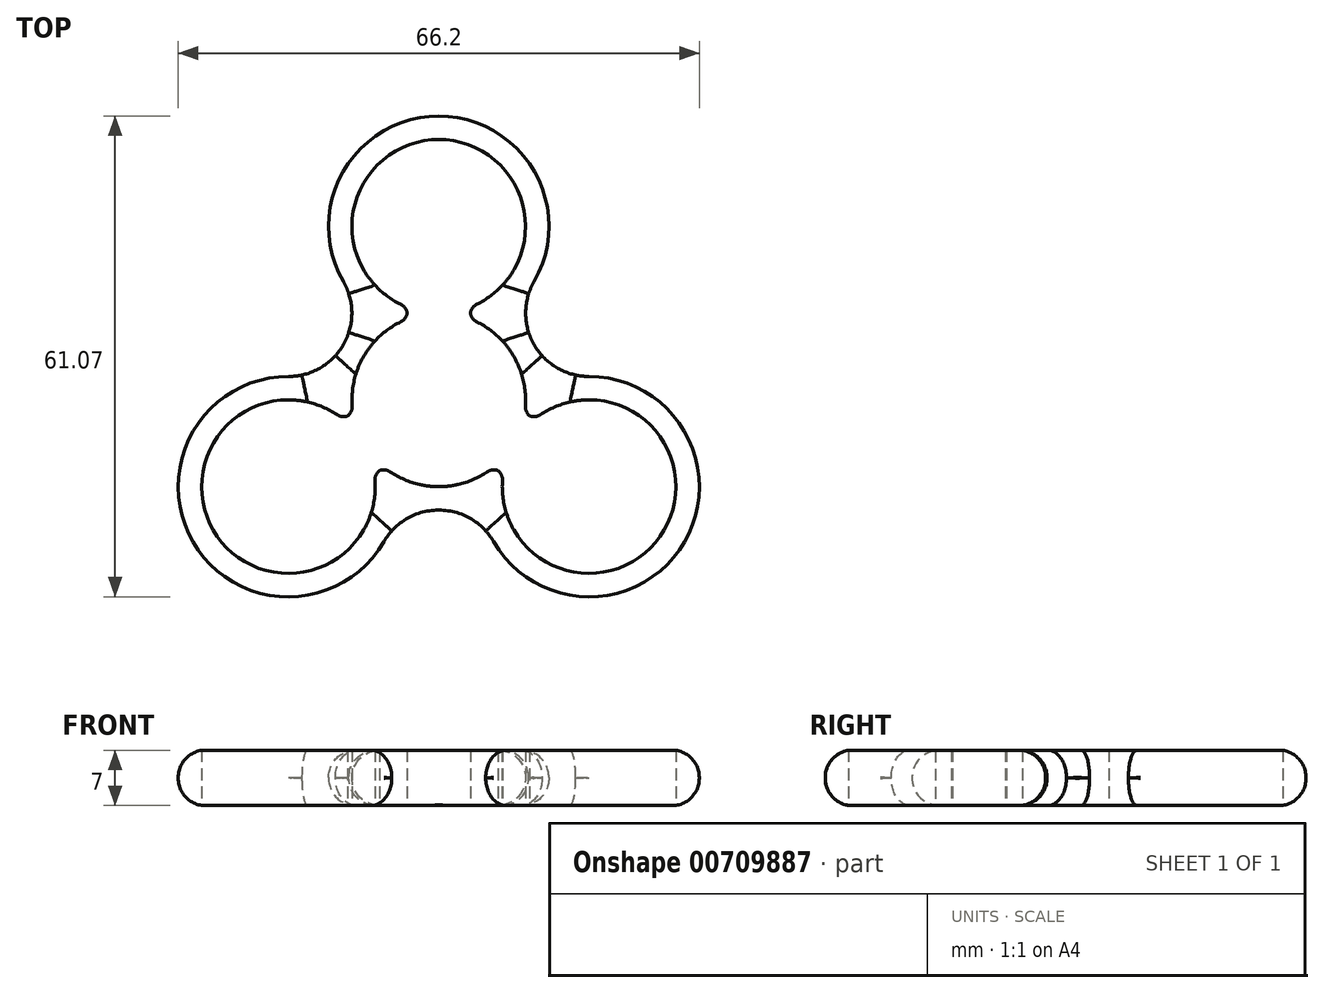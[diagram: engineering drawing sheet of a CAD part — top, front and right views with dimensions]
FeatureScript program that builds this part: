
annotation { "Feature Type Name" : "Feature", "Feature Type Description" : "" }
export const myFeature = defineFeature(function(context is Context, id is Id, definition is map)
    precondition{}
    {
        {
            var Q0;
            Q0=qCreatedBy(makeId("Top.planeOp"),FACE);
            var sketch = newSketch(context, id + "F0", { "sketchPlane" : qUnion([Q0])});
            skArc(sketch, "E0", {"start": v(-4, 10.27) * mm, "mid": v(-9.55, 5.51) * mm, "end": v(-10.9, -1.67) * mm});
            skArc(sketch, "E1", {"start": v(4, 11.78) * mm, "mid": v(0, 33.08) * mm, "end": v(-4, 11.78) * mm});
            skArc(sketch, "E2", {"start": v(4, 8.63) * mm, "mid": v(0, 36.05) * mm, "end": v(-4, 8.63) * mm});
            skArc(sketch, "E3", {"start": v(-4, 13.42) * mm, "mid": v(-12.12, 7) * mm, "end": v(-13.62, -3.24) * mm});
            skLineSegment(sketch, "E4.bottom", {"start": v(4, 7.03) * mm, "end": v(-4, 7.02) * mm});
            skLineSegment(sketch, "E4.top", {"start": v(4, 15.03) * mm, "end": v(-4, 15.03) * mm});
            skLineSegment(sketch, "E4.left", {"start": v(4, 7.03) * mm, "end": v(4, 15.03) * mm});
            skLineSegment(sketch, "E4.right", {"start": v(-4, 7.03) * mm, "end": v(-4, 15.03) * mm});
            skPoint(sketch, "E4.middle", {"position": v(0, 11.03) * mm});
            skArc(sketch, "E5.1.0", {"start": v(-9.48, -0.85) * mm, "mid": v(-31.22, -18.02) * mm, "end": v(-5.48, -7.78) * mm});
            skArc(sketch, "E5.1.1", {"start": v(-12.2, -2.42) * mm, "mid": v(-28.64, -16.54) * mm, "end": v(-8.2, -9.35) * mm});
            skLineSegment(sketch, "E5.1.2", {"start": v(-15.01, -4.05) * mm, "end": v(-11.01, -10.98) * mm});
            skLineSegment(sketch, "E5.1.3", {"start": v(-8.08, -0.05) * mm, "end": v(-15.01, -4.05) * mm});
            skLineSegment(sketch, "E5.1.4", {"start": v(-4.08, -6.98) * mm, "end": v(-11.01, -10.98) * mm});
            skLineSegment(sketch, "E5.1.5", {"start": v(-8.08, -0.05) * mm, "end": v(-4.08, -6.98) * mm});
            skArc(sketch, "E5.2.0", {"start": v(5.48, -7.78) * mm, "mid": v(31.22, -18.03) * mm, "end": v(9.48, -0.85) * mm});
            skArc(sketch, "E5.2.1", {"start": v(8.2, -9.35) * mm, "mid": v(28.64, -16.54) * mm, "end": v(12.2, -2.42) * mm});
            skLineSegment(sketch, "E5.2.2", {"start": v(11.01, -10.98) * mm, "end": v(15.01, -4.05) * mm});
            skLineSegment(sketch, "E5.2.3", {"start": v(4.08, -6.98) * mm, "end": v(11.01, -10.98) * mm});
            skLineSegment(sketch, "E5.2.4", {"start": v(8.08, -0.05) * mm, "end": v(15.01, -4.05) * mm});
            skLineSegment(sketch, "E5.2.5", {"start": v(4.08, -6.98) * mm, "end": v(8.08, -0.05) * mm});
            skArc(sketch, "E6.trimOffspring", {"start": v(-9.62, -10.17) * mm, "mid": v(0, -14) * mm, "end": v(9.62, -10.17) * mm});
            skArc(sketch, "E7.trimOffspring", {"start": v(13.62, -3.24) * mm, "mid": v(12.12, 7) * mm, "end": v(4, 13.42) * mm});
            skArc(sketch, "E8.trimOffspring", {"start": v(10.9, -1.67) * mm, "mid": v(9.55, 5.51) * mm, "end": v(4, 10.27) * mm});
            skArc(sketch, "E9.trimOffspring", {"start": v(-6.9, -8.6) * mm, "mid": v(0, -11.03) * mm, "end": v(6.9, -8.6) * mm});
            skSolve(sketch);
        }
        {
            var Q0;
            {var subQ0=sQuery(id+"F0.wireOp",EDGE,"E3");var subQ1=sQuery(id+"F0.wireOp",EDGE,"E1");var subQ2=makeQuery(id+"F0.imprint","INTERSECT",VERTEX,{"derivedFrom":[subQ1,subQ0]});Q0=makeQuery(id+"F0.imprint","IMPRINT",FACE,{"disambiguationData":[TD([[makeQuery(id+"F0.imprint","IMPRINT",EDGE,{"disambiguationData":[TD([[subQ2,1.0]])],"derivedFrom":subQ1}),-1.0]])]});}
            var Q1;
            {var subQ1=sQuery(id+"F0.wireOp",EDGE,"E0");var subQ5=sQuery(id+"F0.wireOp",EDGE,"E2");var subQ6=makeQuery(id+"F0.imprint","INTERSECT",VERTEX,{"disambiguationData":[OD(0.0)],"derivedFrom":[subQ1,subQ5]});Q1=makeQuery(id+"F0.imprint","IMPRINT",FACE,{"disambiguationData":[TD([[makeQuery(id+"F0.imprint","IMPRINT",EDGE,{"disambiguationData":[TD([[subQ6,-1.0]])],"derivedFrom":subQ1}),-1.0]])]});}
            var Q2;
            {var subQ5=sQuery(id+"F0.wireOp",EDGE,"E4.right");var subQ7=sQuery(id+"F0.wireOp",EDGE,"E0");var subQ8=makeQuery(id+"F0.imprint","INTERSECT",VERTEX,{"derivedFrom":[subQ7,subQ5]});Q2=makeQuery(id+"F0.imprint","IMPRINT",FACE,{"disambiguationData":[TD([[makeQuery(id+"F0.imprint","IMPRINT",EDGE,{"disambiguationData":[TD([[subQ8,-1.0]])],"derivedFrom":subQ7}),-1.0]])]});}
            var Q3;
            {var subQ0=sQuery(id+"F0.wireOp",EDGE,"E2");var subQ1=sQuery(id+"F0.wireOp",EDGE,"E0");var subQ2=makeQuery(id+"F0.imprint","INTERSECT",VERTEX,{"disambiguationData":[OD(0.0)],"derivedFrom":[subQ1,subQ0]});Q3=makeQuery(id+"F0.imprint","IMPRINT",FACE,{"disambiguationData":[TD([[makeQuery(id+"F0.imprint","IMPRINT",EDGE,{"disambiguationData":[TD([[subQ2,1.0]])],"derivedFrom":subQ1}),-1.0]])]});}
            var Q4;
            {var subQ0=sQuery(id+"F0.wireOp",EDGE,"E2");var subQ1=sQuery(id+"F0.wireOp",EDGE,"E0");var subQ2=makeQuery(id+"F0.imprint","INTERSECT",VERTEX,{"disambiguationData":[OD(1.0)],"derivedFrom":[subQ1,subQ0]});Q4=makeQuery(id+"F0.imprint","IMPRINT",FACE,{"disambiguationData":[TD([[makeQuery(id+"F0.imprint","IMPRINT",EDGE,{"disambiguationData":[TD([[subQ2,-1.0]])],"derivedFrom":subQ1}),-1.0]])]});}
            var Q5;
            {var subQ0=sQuery(id+"F0.wireOp",EDGE,"E5.1.0");var subQ1=sQuery(id+"F0.wireOp",EDGE,"E0");var subQ2=makeQuery(id+"F0.imprint","INTERSECT",VERTEX,{"disambiguationData":[OD(1.0)],"derivedFrom":[subQ1,subQ0]});Q5=makeQuery(id+"F0.imprint","IMPRINT",FACE,{"disambiguationData":[TD([[makeQuery(id+"F0.imprint","IMPRINT",EDGE,{"disambiguationData":[TD([[subQ2,-1.0]])],"derivedFrom":subQ1}),-1.0]])]});}
            var Q6;
            {var subQ1=sQuery(id+"F0.wireOp",EDGE,"E0");var subQ5=sQuery(id+"F0.wireOp",EDGE,"E5.2.0");var subQ6=makeQuery(id+"F0.imprint","INTERSECT",VERTEX,{"disambiguationData":[OD(1.0)],"derivedFrom":[subQ1,subQ5]});Q6=makeQuery(id+"F0.imprint","IMPRINT",FACE,{"disambiguationData":[TD([[makeQuery(id+"F0.imprint","IMPRINT",EDGE,{"disambiguationData":[TD([[subQ6,-1.0]])],"derivedFrom":subQ1}),-1.0]])]});}
            var Q7;
            {var subQ1=sQuery(id+"F0.wireOp",EDGE,"E0");var subQ6=sQuery(id+"F0.wireOp",EDGE,"E5.2.0");var subQ8=makeQuery(id+"F0.imprint","INTERSECT",VERTEX,{"disambiguationData":[OD(0.0)],"derivedFrom":[subQ1,subQ6]});Q7=makeQuery(id+"F0.imprint","IMPRINT",FACE,{"disambiguationData":[TD([[makeQuery(id+"F0.imprint","IMPRINT",EDGE,{"disambiguationData":[TD([[subQ8,1.0]])],"derivedFrom":subQ1}),-1.0]])]});}
            var Q8;
            {var subQ0=sQuery(id+"F0.wireOp",EDGE,"E6.trimOffspring");var subQ1=sQuery(id+"F0.wireOp",EDGE,"E5.2.0");var subQ2=makeQuery(id+"F0.imprint","INTERSECT",VERTEX,{"derivedFrom":[subQ1,subQ0]});Q8=makeQuery(id+"F0.imprint","IMPRINT",FACE,{"disambiguationData":[TD([[makeQuery(id+"F0.imprint","IMPRINT",EDGE,{"disambiguationData":[TD([[subQ2,-1.0]])],"derivedFrom":subQ1}),1.0]])]});}
            var Q9;
            {var subQ0=sQuery(id+"F0.wireOp",EDGE,"E5.1.0");var subQ1=sQuery(id+"F0.wireOp",EDGE,"E3");var subQ2=makeQuery(id+"F0.imprint","INTERSECT",VERTEX,{"derivedFrom":[subQ1,subQ0]});Q9=makeQuery(id+"F0.imprint","IMPRINT",FACE,{"disambiguationData":[TD([[makeQuery(id+"F0.imprint","IMPRINT",EDGE,{"disambiguationData":[TD([[subQ2,-1.0]])],"derivedFrom":subQ1}),-1.0]])]});}
            var Q10;
            {var subQ0=sQuery(id+"F0.wireOp",EDGE,"E5.1.4");var subQ5=sQuery(id+"F0.wireOp",EDGE,"E0");var subQ6=makeQuery(id+"F0.imprint","INTERSECT",VERTEX,{"derivedFrom":[subQ5,subQ0]});Q10=makeQuery(id+"F0.imprint","IMPRINT",FACE,{"disambiguationData":[TD([[makeQuery(id+"F0.imprint","IMPRINT",EDGE,{"disambiguationData":[TD([[subQ6,-1.0]])],"derivedFrom":subQ5}),-1.0]])]});}
            var Q11;
            {var subQ5=sQuery(id+"F0.wireOp",EDGE,"E5.1.0");var subQ7=sQuery(id+"F0.wireOp",EDGE,"E0");var subQ8=makeQuery(id+"F0.imprint","INTERSECT",VERTEX,{"disambiguationData":[OD(0.0)],"derivedFrom":[subQ7,subQ5]});Q11=makeQuery(id+"F0.imprint","IMPRINT",FACE,{"disambiguationData":[TD([[makeQuery(id+"F0.imprint","IMPRINT",EDGE,{"disambiguationData":[TD([[subQ8,-1.0]])],"derivedFrom":subQ7}),-1.0]])]});}
            var Q12;
            {var subQ0=sQuery(id+"F0.wireOp",EDGE,"E7.trimOffspring");var subQ1=sQuery(id+"F0.wireOp",EDGE,"E2");var subQ2=makeQuery(id+"F0.imprint","INTERSECT",VERTEX,{"derivedFrom":[subQ1,subQ0]});Q12=makeQuery(id+"F0.imprint","IMPRINT",FACE,{"disambiguationData":[TD([[makeQuery(id+"F0.imprint","IMPRINT",EDGE,{"disambiguationData":[TD([[subQ2,1.0]])],"derivedFrom":subQ1}),-1.0]])]});}
            var Q13;
            {var subQ3=sQuery(id+"F0.wireOp",EDGE,"E1");var subQ5=sQuery(id+"F0.wireOp",EDGE,"E4.left");var subQ6=makeQuery(id+"F0.imprint","INTERSECT",VERTEX,{"derivedFrom":[subQ3,subQ5]});Q13=makeQuery(id+"F0.imprint","IMPRINT",FACE,{"disambiguationData":[TD([[makeQuery(id+"F0.imprint","IMPRINT",EDGE,{"disambiguationData":[TD([[subQ6,-1.0]])],"derivedFrom":subQ3}),-1.0]])]});}
            var Q14;
            {var subQ0=sQuery(id+"F0.wireOp",EDGE,"E7.trimOffspring");var subQ1=sQuery(id+"F0.wireOp",EDGE,"E5.2.0");var subQ2=makeQuery(id+"F0.imprint","INTERSECT",VERTEX,{"derivedFrom":[subQ1,subQ0]});Q14=makeQuery(id+"F0.imprint","IMPRINT",FACE,{"disambiguationData":[TD([[makeQuery(id+"F0.imprint","IMPRINT",EDGE,{"disambiguationData":[TD([[subQ2,-1.0]])],"derivedFrom":subQ1}),1.0]])]});}
            var Q15;
            {var subQ0=sQuery(id+"F0.wireOp",EDGE,"E6.trimOffspring");var subQ1=sQuery(id+"F0.wireOp",EDGE,"E5.2.0");var subQ2=makeQuery(id+"F0.imprint","INTERSECT",VERTEX,{"derivedFrom":[subQ1,subQ0]});Q15=makeQuery(id+"F0.imprint","IMPRINT",FACE,{"disambiguationData":[TD([[makeQuery(id+"F0.imprint","IMPRINT",EDGE,{"disambiguationData":[TD([[subQ2,1.0]])],"derivedFrom":subQ1}),1.0]])]});}
            var Q16;
            {var subQ0=sQuery(id+"F0.wireOp",EDGE,"E6.trimOffspring");var subQ1=sQuery(id+"F0.wireOp",EDGE,"E5.1.0");var subQ2=makeQuery(id+"F0.imprint","INTERSECT",VERTEX,{"derivedFrom":[subQ1,subQ0]});Q16=makeQuery(id+"F0.imprint","IMPRINT",FACE,{"disambiguationData":[TD([[makeQuery(id+"F0.imprint","IMPRINT",EDGE,{"disambiguationData":[TD([[subQ2,-1.0]])],"derivedFrom":subQ1}),-1.0]])]});}
            var Q17;
            {var subQ0=sQuery(id+"F0.wireOp",EDGE,"E6.trimOffspring");var subQ1=sQuery(id+"F0.wireOp",EDGE,"E5.1.0");var subQ2=makeQuery(id+"F0.imprint","INTERSECT",VERTEX,{"derivedFrom":[subQ1,subQ0]});Q17=makeQuery(id+"F0.imprint","IMPRINT",FACE,{"disambiguationData":[TD([[makeQuery(id+"F0.imprint","IMPRINT",EDGE,{"disambiguationData":[TD([[subQ2,-1.0]])],"derivedFrom":subQ1}),1.0]])]});}
            extrude(context, id + "F1", {"entities" : qUnion([Q0, Q1, Q2, Q3, Q4, Q5, Q6, Q7, Q8, Q9, Q10, Q11, Q12, Q13, Q14, Q15, Q16, Q17]), "depth" : 7 * mm, "offsetDistance" : 25 * mm});
        }
        {
            var Q0;
            Q0=makeQuery(id+"F1.opExtrude","SWEPT_EDGE",EDGE,{"disambiguationData":[OSD([sQuery(id+"F0.wireOp",EDGE,"E0"),sQuery(id+"F0.wireOp",EDGE,"E4.right")])]});
            var Q1;
            Q1=makeQuery(id+"F1.opExtrude","SWEPT_EDGE",EDGE,{"disambiguationData":[OSD([sQuery(id+"F0.wireOp",EDGE,"E1"),sQuery(id+"F0.wireOp",EDGE,"E4.right")])]});
            var Q2;
            Q2=makeQuery(id+"F1.opExtrude","SWEPT_EDGE",EDGE,{"disambiguationData":[OSD([sQuery(id+"F0.wireOp",EDGE,"E4.left"),sQuery(id+"F0.wireOp",EDGE,"E8.trimOffspring")])]});
            var Q3;
            Q3=makeQuery(id+"F1.opExtrude","SWEPT_EDGE",EDGE,{"disambiguationData":[OSD([sQuery(id+"F0.wireOp",EDGE,"E1"),sQuery(id+"F0.wireOp",EDGE,"E4.left")])]});
            var Q4;
            Q4=makeQuery(id+"F1.opExtrude","SWEPT_EDGE",EDGE,{"disambiguationData":[OSD([sQuery(id+"F0.wireOp",EDGE,"E0"),sQuery(id+"F0.wireOp",EDGE,"E5.1.3")])]});
            var Q5;
            Q5=makeQuery(id+"F1.opExtrude","SWEPT_EDGE",EDGE,{"disambiguationData":[OSD([sQuery(id+"F0.wireOp",EDGE,"E5.1.1"),sQuery(id+"F0.wireOp",EDGE,"E5.1.3")])]});
            var Q6;
            Q6=makeQuery(id+"F1.opExtrude","SWEPT_EDGE",EDGE,{"disambiguationData":[OSD([sQuery(id+"F0.wireOp",EDGE,"E5.2.4"),sQuery(id+"F0.wireOp",EDGE,"E8.trimOffspring")])]});
            var Q7;
            Q7=makeQuery(id+"F1.opExtrude","SWEPT_EDGE",EDGE,{"disambiguationData":[OSD([sQuery(id+"F0.wireOp",EDGE,"E5.2.1"),sQuery(id+"F0.wireOp",EDGE,"E5.2.4")])]});
            var Q8;
            Q8=makeQuery(id+"F1.opExtrude","SWEPT_EDGE",EDGE,{"disambiguationData":[OSD([sQuery(id+"F0.wireOp",EDGE,"E5.1.4"),sQuery(id+"F0.wireOp",EDGE,"E9.trimOffspring")])]});
            var Q9;
            Q9=makeQuery(id+"F1.opExtrude","SWEPT_EDGE",EDGE,{"disambiguationData":[OSD([sQuery(id+"F0.wireOp",EDGE,"E5.1.1"),sQuery(id+"F0.wireOp",EDGE,"E5.1.4")])]});
            var Q10;
            Q10=makeQuery(id+"F1.opExtrude","SWEPT_EDGE",EDGE,{"disambiguationData":[OSD([sQuery(id+"F0.wireOp",EDGE,"E5.2.3"),sQuery(id+"F0.wireOp",EDGE,"E9.trimOffspring")])]});
            var Q11;
            Q11=makeQuery(id+"F1.opExtrude","SWEPT_EDGE",EDGE,{"disambiguationData":[OSD([sQuery(id+"F0.wireOp",EDGE,"E5.2.1"),sQuery(id+"F0.wireOp",EDGE,"E5.2.3")])]});
            fillet(context, id + "F2", {"entities" : qUnion([Q0, Q1, Q2, Q3, Q4, Q5, Q6, Q7, Q8, Q9, Q10, Q11]), "radius" : 1.5 * mm, "tangentPropagation" : true, "allowEdgeOverflow" : false});
        }
        {
            var Q0;
            Q0=makeQuery(id+"F1.opExtrude","SWEPT_EDGE",EDGE,{"disambiguationData":[OSD([sQuery(id+"F0.wireOp",EDGE,"E2"),sQuery(id+"F0.wireOp",EDGE,"E3")])]});
            var Q1;
            Q1=makeQuery(id+"F1.opExtrude","SWEPT_EDGE",EDGE,{"disambiguationData":[OSD([sQuery(id+"F0.wireOp",EDGE,"E2"),sQuery(id+"F0.wireOp",EDGE,"E7.trimOffspring")])]});
            var Q2;
            Q2=makeQuery(id+"F1.opExtrude","SWEPT_EDGE",EDGE,{"disambiguationData":[OSD([sQuery(id+"F0.wireOp",EDGE,"E5.2.0"),sQuery(id+"F0.wireOp",EDGE,"E7.trimOffspring")])]});
            var Q3;
            Q3=makeQuery(id+"F1.opExtrude","SWEPT_EDGE",EDGE,{"disambiguationData":[OSD([sQuery(id+"F0.wireOp",EDGE,"E5.2.0"),sQuery(id+"F0.wireOp",EDGE,"E6.trimOffspring")])]});
            var Q4;
            Q4=makeQuery(id+"F1.opExtrude","SWEPT_EDGE",EDGE,{"disambiguationData":[OSD([sQuery(id+"F0.wireOp",EDGE,"E5.1.0"),sQuery(id+"F0.wireOp",EDGE,"E6.trimOffspring")])]});
            var Q5;
            Q5=makeQuery(id+"F1.opExtrude","SWEPT_EDGE",EDGE,{"disambiguationData":[OSD([sQuery(id+"F0.wireOp",EDGE,"E3"),sQuery(id+"F0.wireOp",EDGE,"E5.1.0")])]});
            fillet(context, id + "F3", {"entities" : qUnion([Q0, Q1, Q2, Q3, Q4, Q5]), "radius" : 8 * mm, "tangentPropagation" : true, "allowEdgeOverflow" : false});
        }
        {
            var Q0;
            Q0=makeQuery(id+"F1.opExtrude","CAP_EDGE",EDGE,{"disambiguationData":[OSD([sQuery(id+"F0.wireOp",EDGE,"E2")])],"isStart":false});
            var Q1;
            Q1=makeQuery(id+"F1.opExtrude","CAP_EDGE",EDGE,{"disambiguationData":[OSD([sQuery(id+"F0.wireOp",EDGE,"E2")])],"isStart":true});
            fillet(context, id + "F4", {"entities" : qUnion([Q0, Q1]), "radius" : 3.5 * mm, "tangentPropagation" : true, "allowEdgeOverflow" : false});
        }
    });
